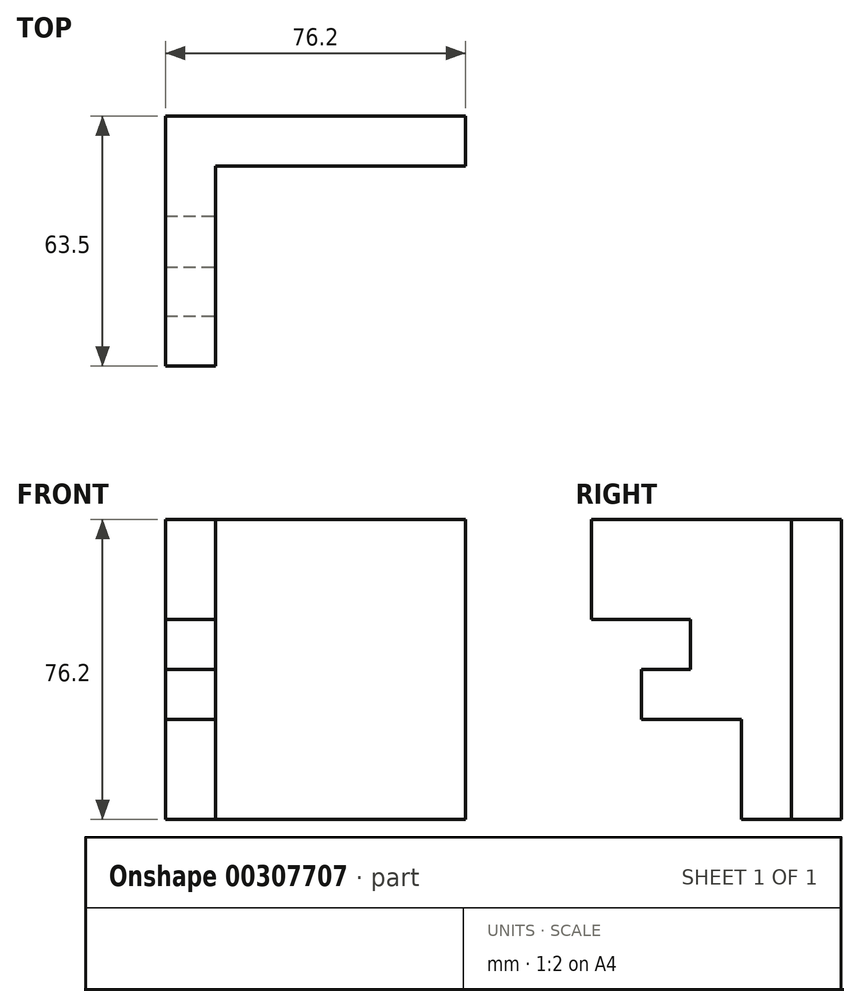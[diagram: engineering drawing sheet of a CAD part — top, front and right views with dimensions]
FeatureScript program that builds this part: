
annotation { "Feature Type Name" : "Feature", "Feature Type Description" : "" }
export const myFeature = defineFeature(function(context is Context, id is Id, definition is map)
    precondition{}
    {
        {
            var Q0;
            Q0=qCreatedBy(makeId("Top.planeOp"),FACE);
            var sketch = newSketch(context, id + "F0", { "sketchPlane" : qUnion([Q0])});
            skLineSegment(sketch, "E0", {"start": v(-42.9, -40.74) * mm, "end": v(-42.9, -15.34) * mm});
            skLineSegment(sketch, "E1", {"start": v(-42.9, -15.34) * mm, "end": v(33.3, -15.34) * mm});
            skLineSegment(sketch, "E2", {"start": v(33.3, -15.34) * mm, "end": v(33.3, -28.04) * mm});
            skLineSegment(sketch, "E3", {"start": v(33.3, -28.04) * mm, "end": v(-30.2, -28.04) * mm});
            skLineSegment(sketch, "E4", {"start": v(-30.2, -28.04) * mm, "end": v(-30.2, -40.74) * mm});
            skLineSegment(sketch, "E5", {"start": v(-30.2, -40.74) * mm, "end": v(-42.9, -40.74) * mm});
            skSolve(sketch);
        }
        {
            var Q0;
            Q0=makeQuery(id+"F0.imprint","IMPRINT",FACE,{"disambiguationData":[TD([[makeQuery(id+"F0.imprint","IMPRINT",EDGE,{"derivedFrom":sQuery(id+"F0.wireOp",EDGE,"E0")}),-1.0]])]});
            extrude(context, id + "F1", {"entities" : qUnion([Q0]), "depth" : 76.2 * mm});
        }
        {
            var Q0;
            Q0=makeQuery(id+"F1.opExtrude","SWEPT_FACE",FACE,{"disambiguationData":[OSD([sQuery(id+"F0.wireOp",EDGE,"E4")])]});
            var sketch = newSketch(context, id + "F2", { "sketchPlane" : qUnion([Q0])});
            skLineSegment(sketch, "E6", {"start": v(-28.04, 76.2) * mm, "end": v(-78.84, 76.2) * mm});
            skLineSegment(sketch, "E7", {"start": v(-78.84, 76.2) * mm, "end": v(-78.84, 50.8) * mm});
            skLineSegment(sketch, "E8", {"start": v(-78.84, 50.8) * mm, "end": v(-53.71, 50.8) * mm});
            skLineSegment(sketch, "E9", {"start": v(-53.71, 50.8) * mm, "end": v(-53.71, 38.1) * mm});
            skLineSegment(sketch, "E10", {"start": v(-53.71, 38.1) * mm, "end": v(-66.14, 38.1) * mm});
            skLineSegment(sketch, "E11", {"start": v(-66.14, 38.1) * mm, "end": v(-66.14, 25.4) * mm});
            skLineSegment(sketch, "E12", {"start": v(-66.14, 25.4) * mm, "end": v(-40.74, 25.4) * mm});
            skPoint(sketch, "E12.endSnap0", {"position": v(-40.74, 38.1) * mm});
            skSolve(sketch);
        }
        {
            var Q0;
            {var subQ0=sQuery(id+"F2.wireOp",EDGE,"E7");Q0=makeQuery(id+"F2.imprint","IMPRINT",FACE,{"disambiguationData":[TD([[makeQuery(id+"F2.imprint","IMPRINT",EDGE,{"derivedFrom":subQ0}),1.0]])]});}
            extrude(context, id + "F3", {"entities" : qUnion([Q0]), "operationType" : NewBodyOperationType.ADD, "oppositeDirection" : true, "depth" : 12.7 * mm});
        }
    });
